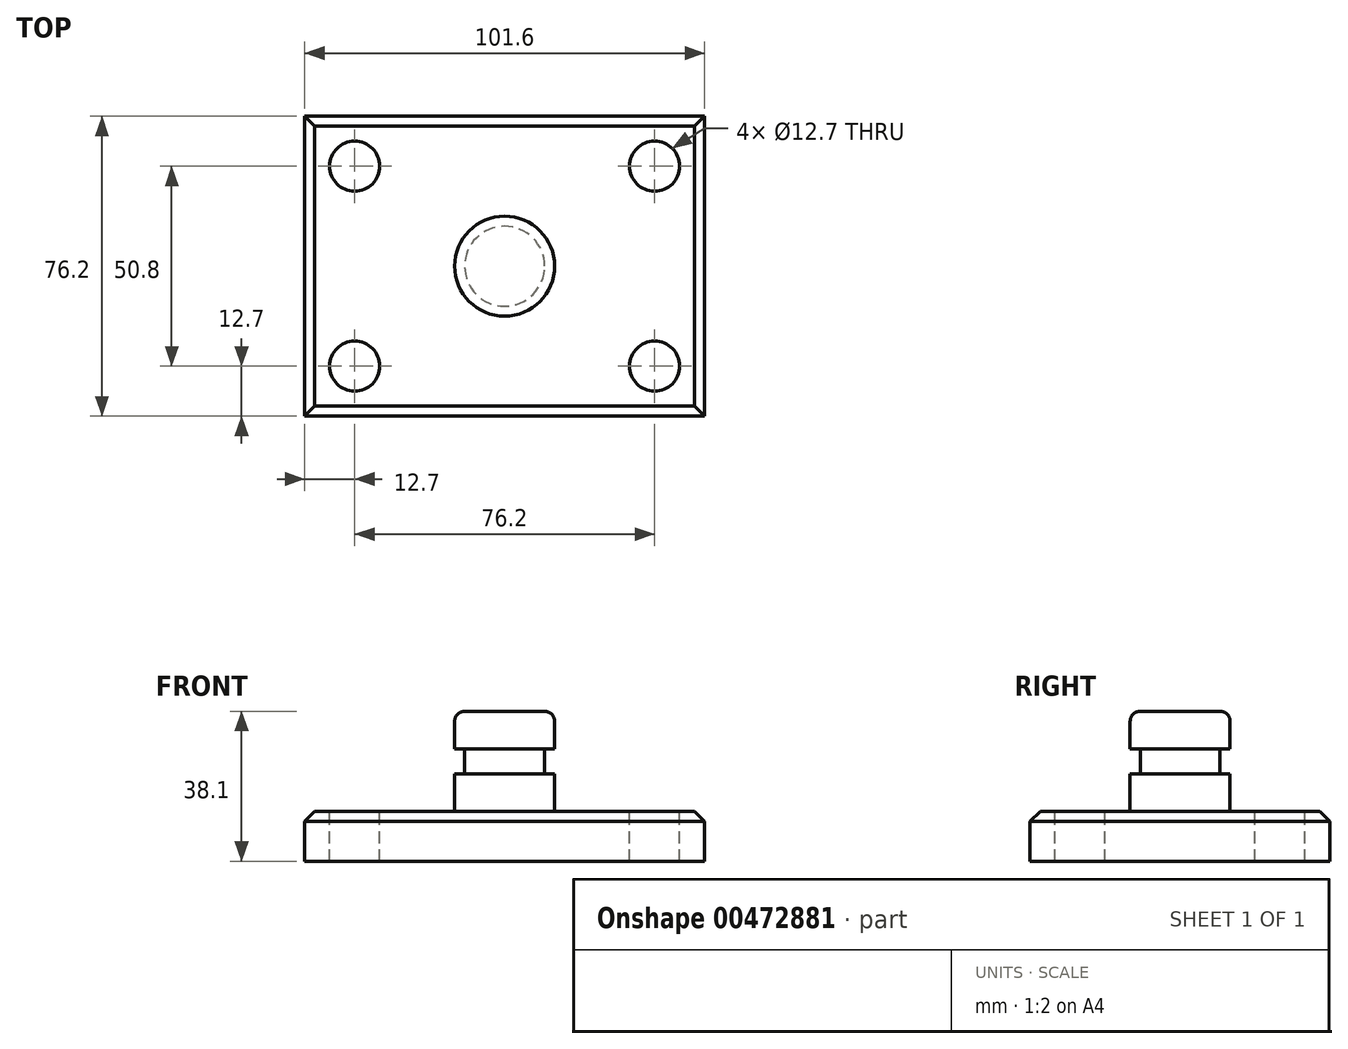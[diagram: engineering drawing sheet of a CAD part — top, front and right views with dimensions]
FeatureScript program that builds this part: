
annotation { "Feature Type Name" : "Feature", "Feature Type Description" : "" }
export const myFeature = defineFeature(function(context is Context, id is Id, definition is map)
    precondition{}
    {
        {
            var Q0;
            Q0=qCreatedBy(makeId("Top.planeOp"),FACE);
            var sketch = newSketch(context, id + "F0", { "sketchPlane" : qUnion([Q0])});
            skLineSegment(sketch, "E0.bottom", {"start": v(50.8, 38.1) * mm, "end": v(-50.8, 38.1) * mm});
            skLineSegment(sketch, "E0.top", {"start": v(50.8, -38.1) * mm, "end": v(-50.8, -38.1) * mm});
            skLineSegment(sketch, "E0.left", {"start": v(50.8, 38.1) * mm, "end": v(50.8, -38.1) * mm});
            skLineSegment(sketch, "E0.right", {"start": v(-50.8, 38.1) * mm, "end": v(-50.8, -38.1) * mm});
            skPoint(sketch, "E0.middle", {"position": v(0, 0) * mm});
            skSolve(sketch);
        }
        {
            var Q0;
            Q0=makeQuery(id+"F0.imprint","IMPRINT",FACE,{"disambiguationData":[TD([[makeQuery(id+"F0.imprint","IMPRINT",EDGE,{"derivedFrom":sQuery(id+"F0.wireOp",EDGE,"E0.bottom")}),1.0]])]});
            extrude(context, id + "F1", {"entities" : qUnion([Q0]), "depth" : 12.7 * mm});
        }
        {
            var Q0;
            Q0=makeQuery(id+"F1.opExtrude","CAP_FACE",FACE,{"disambiguationData":[OSD([sQuery(id+"F0.wireOp",EDGE,"E0.bottom"),sQuery(id+"F0.wireOp",EDGE,"E0.top"),sQuery(id+"F0.wireOp",EDGE,"E0.left"),sQuery(id+"F0.wireOp",EDGE,"E0.right")])],"isStart":false});
            var sketch = newSketch(context, id + "F2", { "sketchPlane" : qUnion([Q0])});
            skCircle(sketch, "E1", {"center": v(-38.1, 25.4) * mm, "radius": 6.35 * mm});
            skCircle(sketch, "E2", {"center": v(-38.1, -25.4) * mm, "radius": 6.35 * mm});
            skCircle(sketch, "E3", {"center": v(38.1, 25.4) * mm, "radius": 6.35 * mm});
            skCircle(sketch, "E4", {"center": v(38.1, -25.4) * mm, "radius": 6.35 * mm});
            skSolve(sketch);
        }
        {
            var Q0;
            Q0=makeQuery(id+"F2.imprint","IMPRINT",FACE,{"disambiguationData":[TD([[makeQuery(id+"F2.imprint","IMPRINT",EDGE,{"derivedFrom":sQuery(id+"F2.wireOp",EDGE,"E1")}),1.0]])]});
            var Q1;
            Q1=makeQuery(id+"F2.imprint","IMPRINT",FACE,{"disambiguationData":[TD([[makeQuery(id+"F2.imprint","IMPRINT",EDGE,{"derivedFrom":sQuery(id+"F2.wireOp",EDGE,"E2")}),1.0]])]});
            var Q2;
            Q2=makeQuery(id+"F2.imprint","IMPRINT",FACE,{"disambiguationData":[TD([[makeQuery(id+"F2.imprint","IMPRINT",EDGE,{"derivedFrom":sQuery(id+"F2.wireOp",EDGE,"E4")}),1.0]])]});
            var Q3;
            Q3=makeQuery(id+"F2.imprint","IMPRINT",FACE,{"disambiguationData":[TD([[makeQuery(id+"F2.imprint","IMPRINT",EDGE,{"derivedFrom":sQuery(id+"F2.wireOp",EDGE,"E3")}),1.0]])]});
            extrude(context, id + "F3", {"entities" : qUnion([Q0, Q1, Q2, Q3]), "operationType" : NewBodyOperationType.REMOVE, "endBound" : BoundingType.THROUGH_ALL, "oppositeDirection" : true, "depth" : 25.4 * mm});
        }
        {
            var Q0;
            Q0=qCreatedBy(makeId("Front.planeOp"),FACE);
            var sketch = newSketch(context, id + "F4", { "sketchPlane" : qUnion([Q0])});
            skLineSegment(sketch, "E5.bottom", {"start": v(0, 12.7) * mm, "end": v(12.7, 12.7) * mm});
            skLineSegment(sketch, "E5.top", {"start": v(0, 38.1) * mm, "end": v(12.7, 38.1) * mm});
            skLineSegment(sketch, "E5.left", {"start": v(0, 12.7) * mm, "end": v(0, 38.1) * mm});
            skLineSegment(sketch, "E5.right", {"start": v(12.7, 12.7) * mm, "end": v(12.7, 38.1) * mm});
            skSolve(sketch);
        }
        {
            var Q0;
            Q0=makeQuery(id+"F4.imprint","IMPRINT",FACE,{"disambiguationData":[TD([[makeQuery(id+"F4.imprint","IMPRINT",EDGE,{"derivedFrom":sQuery(id+"F4.wireOp",EDGE,"E5.bottom")}),1.0]])]});
            var Q1;
            Q1=sQuery(id+"F4.wireOp",EDGE,"E5.left");
            revolve(context, id + "F5", {"operationType" : NewBodyOperationType.ADD, "entities" : qUnion([Q0]), "axis" : qUnion([Q1]), "revolveType" : RevolveType.FULL});
        }
        {
            var Q0;
            Q0=qCreatedBy(makeId("Front.planeOp"),FACE);
            var sketch = newSketch(context, id + "F6", { "sketchPlane" : qUnion([Q0])});
            skLineSegment(sketch, "E6.bottom", {"start": v(16.51, 28.53) * mm, "end": v(10.16, 28.53) * mm});
            skLineSegment(sketch, "E6.top", {"start": v(16.51, 22.18) * mm, "end": v(10.16, 22.18) * mm});
            skLineSegment(sketch, "E6.left", {"start": v(16.51, 28.53) * mm, "end": v(16.51, 22.18) * mm});
            skLineSegment(sketch, "E6.right", {"start": v(10.16, 28.53) * mm, "end": v(10.16, 22.18) * mm});
            skSolve(sketch);
        }
        {
            var Q0;
            Q0=makeQuery(id+"F6.imprint","IMPRINT",FACE,{"disambiguationData":[TD([[makeQuery(id+"F6.imprint","IMPRINT",EDGE,{"derivedFrom":sQuery(id+"F6.wireOp",EDGE,"E6.bottom")}),1.0]])]});
            var Q1;
            Q1=makeQuery(id+"F5.opRevolve","SWEPT_FACE",FACE,{"disambiguationData":[OSD([sQuery(id+"F4.wireOp",EDGE,"E5.right")])]});
            revolve(context, id + "F7", {"operationType" : NewBodyOperationType.REMOVE, "entities" : qUnion([Q0]), "axis" : qUnion([Q1]), "revolveType" : RevolveType.FULL, "oppositeDirection" : true});
        }
        {
            var Q0;
            Q0=makeQuery(id+"F5.opRevolve","SWEPT_EDGE",EDGE,{"disambiguationData":[OSD([sQuery(id+"F4.wireOp",EDGE,"E5.bottom"),sQuery(id+"F4.wireOp",EDGE,"E5.right")])]});
            var Q1;
            Q1=makeQuery(id+"F5.opRevolve","SWEPT_EDGE",EDGE,{"disambiguationData":[OSD([sQuery(id+"F4.wireOp",EDGE,"E5.top"),sQuery(id+"F4.wireOp",EDGE,"E5.right")])]});
            fillet(context, id + "F8", {"entities" : qUnion([Q0, Q1]), "radius" : 2.54 * mm, "tangentPropagation" : true, "allowEdgeOverflow" : false});
        }
        {
            var Q0;
            Q0=makeQuery(id+"F1.opExtrude","CAP_EDGE",EDGE,{"disambiguationData":[OSD([sQuery(id+"F0.wireOp",EDGE,"E0.left")])],"isStart":false});
            var Q1;
            Q1=makeQuery(id+"F1.opExtrude","CAP_EDGE",EDGE,{"disambiguationData":[OSD([sQuery(id+"F0.wireOp",EDGE,"E0.bottom")])],"isStart":false});
            var Q2;
            Q2=makeQuery(id+"F1.opExtrude","CAP_EDGE",EDGE,{"disambiguationData":[OSD([sQuery(id+"F0.wireOp",EDGE,"E0.right")])],"isStart":false});
            var Q3;
            Q3=makeQuery(id+"F1.opExtrude","CAP_EDGE",EDGE,{"disambiguationData":[OSD([sQuery(id+"F0.wireOp",EDGE,"E0.top")])],"isStart":false});
            chamfer(context, id + "F9", {"entities" : qUnion([Q0, Q1, Q2, Q3]), "width" : 2.54 * mm, "tangentPropagation" : true});
        }
    });
